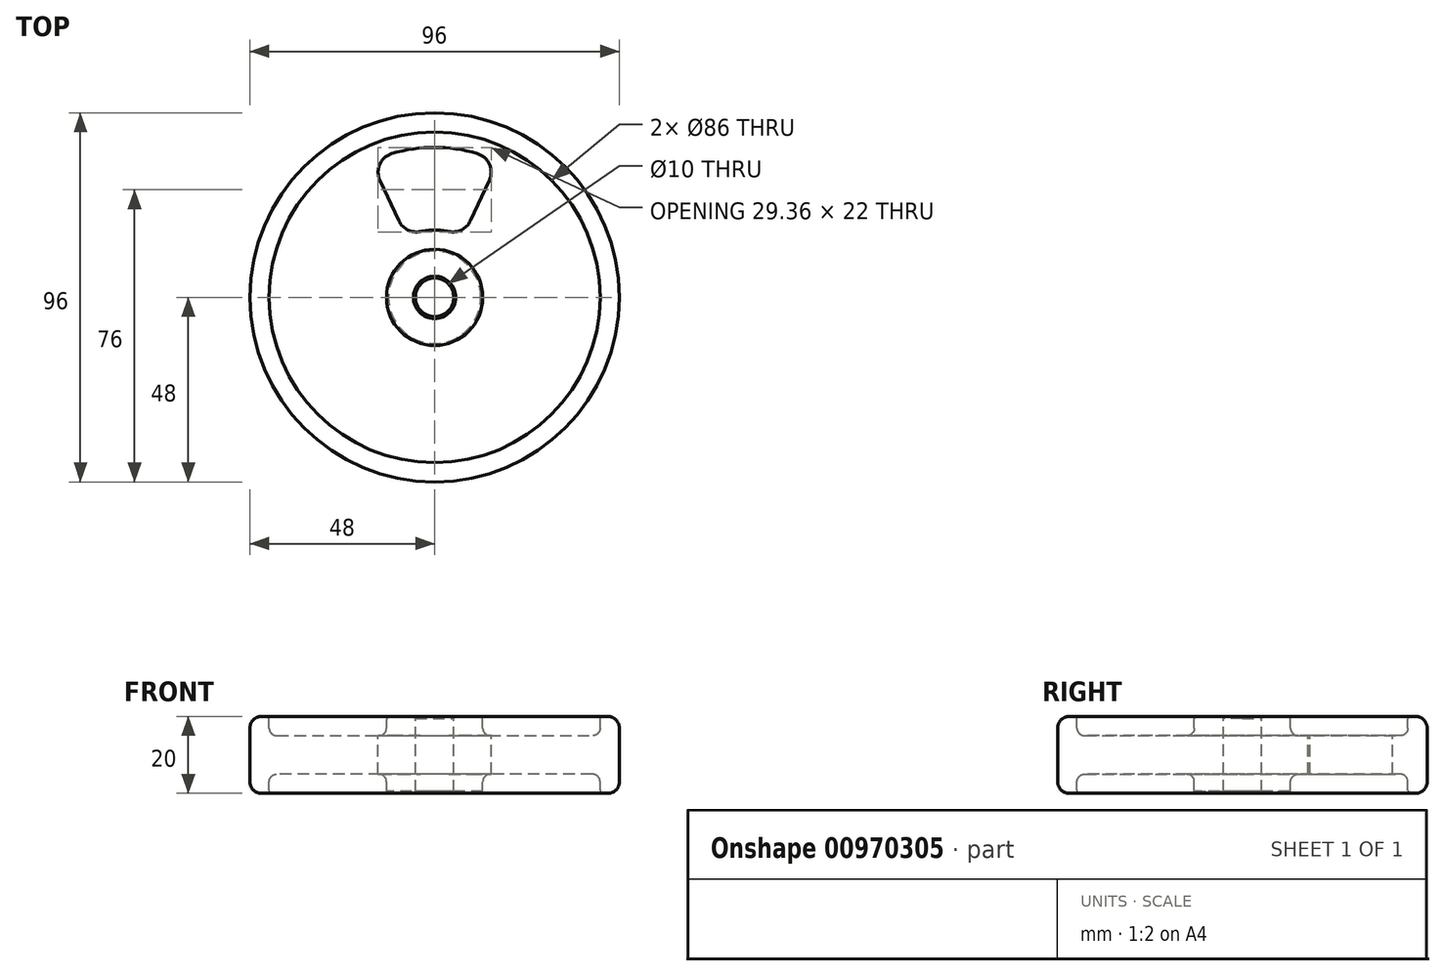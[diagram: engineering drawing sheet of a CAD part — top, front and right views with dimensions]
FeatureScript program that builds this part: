
annotation { "Feature Type Name" : "Feature", "Feature Type Description" : "" }
export const myFeature = defineFeature(function(context is Context, id is Id, definition is map)
    precondition{}
    {
        {
            var Q0;
            Q0=qCreatedBy(makeId("Front.planeOp"),FACE);
            var sketch = newSketch(context, id + "F0", { "sketchPlane" : qUnion([Q0])});
            skLineSegment(sketch, "E0", {"start": v(-5, 0) * mm, "end": v(-5, -20) * mm});
            skLineSegment(sketch, "E1", {"start": v(-5, -20) * mm, "end": v(-12.5, -20) * mm});
            skLineSegment(sketch, "E2", {"start": v(-12.5, -20) * mm, "end": v(-12.5, -15) * mm});
            skLineSegment(sketch, "E3", {"start": v(-12.5, -15) * mm, "end": v(-43, -15) * mm});
            skLineSegment(sketch, "E4", {"start": v(-43, -15) * mm, "end": v(-43, -20) * mm});
            skLineSegment(sketch, "E5", {"start": v(-43, -20) * mm, "end": v(-48, -20) * mm});
            skLineSegment(sketch, "E6", {"start": v(-48, -20) * mm, "end": v(-48, 0) * mm});
            skLineSegment(sketch, "E7", {"start": v(-48, 0) * mm, "end": v(-43, 0) * mm});
            skLineSegment(sketch, "E8", {"start": v(-43, 0) * mm, "end": v(-43, -5) * mm});
            skLineSegment(sketch, "E9", {"start": v(-43, -5) * mm, "end": v(-12.5, -5) * mm});
            skLineSegment(sketch, "E10", {"start": v(-12.5, -5) * mm, "end": v(-12.5, 0) * mm});
            skLineSegment(sketch, "E11", {"start": v(-12.5, 0) * mm, "end": v(-5, 0) * mm});
            skPoint(sketch, "E12.end.orphan", {"position": v(-12.5, -2.5) * mm});
            skLineSegment(sketch, "E13", {"start": v(0, 0) * mm, "end": v(0, -17.94) * mm});
            skSolve(sketch);
        }
        {
            var Q0;
            Q0=makeQuery(id+"F0.imprint","IMPRINT",FACE,{"disambiguationData":[TD([[makeQuery(id+"F0.imprint","IMPRINT",EDGE,{"derivedFrom":sQuery(id+"F0.wireOp",EDGE,"E0")}),-1.0]])]});
            var Q1;
            Q1=sQuery(id+"F0.wireOp",EDGE,"E13");
            revolve(context, id + "F1", {"surfaceOperationType" : NewSurfaceOperationType.NEW, "entities" : qUnion([Q0]), "axis" : qUnion([Q1]), "revolveType" : RevolveType.FULL});
        }
        {
            var Q0;
            Q0=makeQuery(id+"F1.opRevolve","SWEPT_EDGE",EDGE,{"disambiguationData":[OSD([sQuery(id+"F0.wireOp",EDGE,"E9"),sQuery(id+"F0.wireOp",EDGE,"E10")])]});
            var Q1;
            Q1=makeQuery(id+"F1.opRevolve","SWEPT_EDGE",EDGE,{"disambiguationData":[OSD([sQuery(id+"F0.wireOp",EDGE,"E8"),sQuery(id+"F0.wireOp",EDGE,"E9")])]});
            var Q2;
            Q2=makeQuery(id+"F1.opRevolve","SWEPT_EDGE",EDGE,{"disambiguationData":[OSD([sQuery(id+"F0.wireOp",EDGE,"E2"),sQuery(id+"F0.wireOp",EDGE,"E3")])]});
            var Q3;
            Q3=makeQuery(id+"F1.opRevolve","SWEPT_EDGE",EDGE,{"disambiguationData":[OSD([sQuery(id+"F0.wireOp",EDGE,"E3"),sQuery(id+"F0.wireOp",EDGE,"E4")])]});
            fillet(context, id + "F2", {"entities" : qUnion([Q0, Q1, Q2, Q3]), "radius" : 2 * mm, "tangentPropagation" : true, "allowEdgeOverflow" : false});
        }
        {
            var Q0;
            Q0=makeQuery(id+"F1.opRevolve","SWEPT_EDGE",EDGE,{"disambiguationData":[OSD([sQuery(id+"F0.wireOp",EDGE,"E6"),sQuery(id+"F0.wireOp",EDGE,"E7")])]});
            var Q1;
            Q1=makeQuery(id+"F1.opRevolve","SWEPT_EDGE",EDGE,{"disambiguationData":[OSD([sQuery(id+"F0.wireOp",EDGE,"E5"),sQuery(id+"F0.wireOp",EDGE,"E6")])]});
            fillet(context, id + "F3", {"entities" : qUnion([Q0, Q1]), "radius" : 3 * mm, "tangentPropagation" : true, "allowEdgeOverflow" : false});
        }
        {
            var Q0;
            Q0=makeQuery(id+"F1.opRevolve","SWEPT_FACE",FACE,{"disambiguationData":[OSD([sQuery(id+"F0.wireOp",EDGE,"E1")])]});
            var Q1;
            Q1=makeQuery(id+"F1.opRevolve","SWEPT_FACE",FACE,{"disambiguationData":[OSD([sQuery(id+"F0.wireOp",EDGE,"E0")])]});
            chamfer(context, id + "F4", {"entities" : qUnion([Q0, Q1]), "width" : .5 * mm, "tangentPropagation" : true});
        }
        {
            var Q0;
            Q0=makeQuery(id+"F1.opRevolve","SWEPT_FACE",FACE,{"disambiguationData":[OSD([sQuery(id+"F0.wireOp",EDGE,"E4")])]});
            var Q1;
            Q1=makeQuery(id+"F1.opRevolve","SWEPT_FACE",FACE,{"disambiguationData":[OSD([sQuery(id+"F0.wireOp",EDGE,"E8")])]});
            var Q2;
            Q2=makeQuery(id+"F1.opRevolve","SWEPT_EDGE",EDGE,{"disambiguationData":[OSD([sQuery(id+"F0.wireOp",EDGE,"E1"),sQuery(id+"F0.wireOp",EDGE,"E2")])]});
            var Q3;
            Q3=makeQuery(id+"F1.opRevolve","SWEPT_EDGE",EDGE,{"disambiguationData":[OSD([sQuery(id+"F0.wireOp",EDGE,"E10"),sQuery(id+"F0.wireOp",EDGE,"E11")])]});
            fillet(context, id + "F5", {"entities" : qUnion([Q0, Q1, Q2, Q3]), "radius" : .75 * mm, "tangentPropagation" : true, "allowEdgeOverflow" : false});
        }
        {
            var Q0;
            Q0=qCreatedBy(makeId("Top.planeOp"),FACE);
            var sketch = newSketch(context, id + "F6", { "sketchPlane" : qUnion([Q0])});
            skPoint(sketch, "E14.center", {"position": v(0, 0) * mm});
            skLineSegment(sketch, "E15", {"start": v(-14.21, 30.48) * mm, "end": v(-9.27, 19.88) * mm});
            skLineSegment(sketch, "E16", {"start": v(9.27, 19.88) * mm, "end": v(14.21, 30.48) * mm});
            skArc(sketch, "E17", {"start": v(11.1, 37.39) * mm, "mid": v(0, 39) * mm, "end": v(-11.1, 37.39) * mm});
            skArc(sketch, "E18", {"start": v(3.69, 17.1) * mm, "mid": v(0, 17.5) * mm, "end": v(-3.69, 17.1) * mm});
            skArc(sketch, "E19.filletArc", {"start": v(-11.1, 37.39) * mm, "mid": v(-14.24, 34.64) * mm, "end": v(-14.21, 30.48) * mm});
            skArc(sketch, "E20.filletArc", {"start": v(14.21, 30.48) * mm, "mid": v(14.24, 34.64) * mm, "end": v(11.1, 37.39) * mm});
            skArc(sketch, "E21.filletArc", {"start": v(3.69, 17.1) * mm, "mid": v(6.96, 17.52) * mm, "end": v(9.27, 19.88) * mm});
            skArc(sketch, "E22.filletArc", {"start": v(-9.27, 19.88) * mm, "mid": v(-6.96, 17.52) * mm, "end": v(-3.69, 17.1) * mm});
            skSolve(sketch);
        }
        {
            var Q0;
            Q0=qCreatedBy(makeId("Right.planeOp"),FACE);
            var sketch = newSketch(context, id + "F7", { "sketchPlane" : qUnion([Q0])});
            skLineSegment(sketch, "E23", {"start": v(0, 0) * mm, "end": v(0, -31.6) * mm});
            skSolve(sketch);
        }
        {
            var Q0;
            Q0 = qSketchRegion(id + "F6", true);
            var Q1;
            Q1=makeQuery(id+"F3xeonLiqdhliLR_1.4.F6.imprint","IMPRINT",FACE,{"disambiguationData":[TD([[makeQuery(id+"F3xeonLiqdhliLR_1.4.F6.imprint","IMPRINT",EDGE,{"derivedFrom":sQuery(id+"F3xeonLiqdhliLR_1.4.F6.wireOp",EDGE,"E15")}),1.0]])]});
            var Q2;
            Q2=makeQuery(id+"F3xeonLiqdhliLR_1.3.F6.imprint","IMPRINT",FACE,{"disambiguationData":[TD([[makeQuery(id+"F3xeonLiqdhliLR_1.3.F6.imprint","IMPRINT",EDGE,{"derivedFrom":sQuery(id+"F3xeonLiqdhliLR_1.3.F6.wireOp",EDGE,"E15")}),1.0]])]});
            var Q3;
            Q3=makeQuery(id+"F3xeonLiqdhliLR_1.2.F6.imprint","IMPRINT",FACE,{"disambiguationData":[TD([[makeQuery(id+"F3xeonLiqdhliLR_1.2.F6.imprint","IMPRINT",EDGE,{"derivedFrom":sQuery(id+"F3xeonLiqdhliLR_1.2.F6.wireOp",EDGE,"E15")}),1.0]])]});
            var Q4;
            Q4=makeQuery(id+"F3xeonLiqdhliLR_1.1.F6.imprint","IMPRINT",FACE,{"disambiguationData":[TD([[makeQuery(id+"F3xeonLiqdhliLR_1.1.F6.imprint","IMPRINT",EDGE,{"derivedFrom":sQuery(id+"F3xeonLiqdhliLR_1.1.F6.wireOp",EDGE,"E15")}),1.0]])]});
            extrude(context, id + "F8", {"entities" : qUnion([Q0, Q1, Q2, Q3, Q4]), "operationType" : NewBodyOperationType.REMOVE, "endBound" : BoundingType.THROUGH_ALL, "oppositeDirection" : true, "depth" : 25 * mm, "offsetDistance" : 25 * mm});
        }
    });
